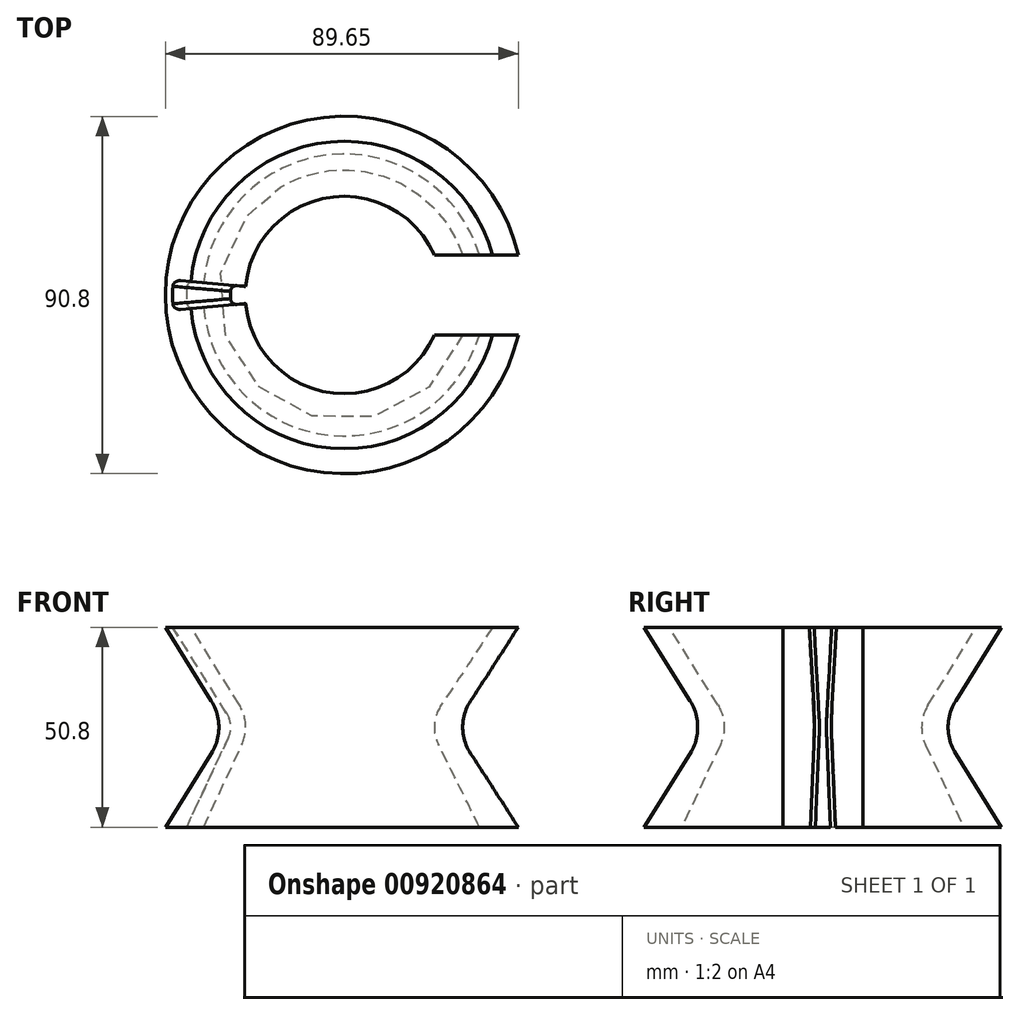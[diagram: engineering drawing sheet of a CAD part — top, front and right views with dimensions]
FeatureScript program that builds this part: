
annotation { "Feature Type Name" : "Feature", "Feature Type Description" : "" }
export const myFeature = defineFeature(function(context is Context, id is Id, definition is map)
    precondition{}
    {
        {
            var Q0;
            Q0=qCreatedBy(makeId("Front.planeOp"),FACE);
            var sketch = newSketch(context, id + "F0", { "sketchPlane" : qUnion([Q0])});
            skLineSegment(sketch, "E0", {"start": v(25.08, -16.33) * mm, "end": v(25.08, 0) * mm, "construction": true});
            skArc(sketch, "E1", {"start": v(26.7, 5.62) * mm, "mid": v(25.1, 0.65) * mm, "end": v(26.08, -4.48) * mm});
            skLineSegment(sketch, "E2", {"start": v(39.05, 25.4) * mm, "end": v(26.7, 5.62) * mm});
            skLineSegment(sketch, "E3", {"start": v(35.83, -25.4) * mm, "end": v(26.08, -4.48) * mm});
            skLineSegment(sketch, "E4", {"start": v(39.05, 25.4) * mm, "end": v(45.4, 25.4) * mm});
            skLineSegment(sketch, "E5", {"start": v(45.4, 25.4) * mm, "end": v(45.4, -25.4) * mm, "construction": true});
            skLineSegment(sketch, "E6", {"start": v(45.4, -25.4) * mm, "end": v(35.83, -25.4) * mm});
            skLineSegment(sketch, "E7", {"start": v(0, 56.75) * mm, "end": v(0, -54.17) * mm, "construction": true});
            skLineSegment(sketch, "E8", {"start": v(45.4, 25.4) * mm, "end": v(33.74, 6.73) * mm});
            skLineSegment(sketch, "E9", {"start": v(33.74, -6.73) * mm, "end": v(45.4, -25.4) * mm});
            skPoint(sketch, "E10.visualSharp", {"position": v(29.53, 0) * mm});
            skArc(sketch, "E10.filletArc", {"start": v(33.74, 6.73) * mm, "mid": v(31.8, 0) * mm, "end": v(33.74, -6.73) * mm});
            skSolve(sketch);
        }
        {
            var Q0;
            Q0 = qSketchRegion(id + "F0", true);
            var Q1;
            Q1=sQuery(id+"F0.wireOp",EDGE,"E7");
            revolve(context, id + "F1", {"surfaceOperationType" : NewSurfaceOperationType.NEW, "entities" : qUnion([Q0]), "axis" : qUnion([Q1]), "revolveType" : RevolveType.FULL});
        }
        {
            var Q0;
            Q0=qCreatedBy(makeId("Front.planeOp"),FACE);
            var sketch = newSketch(context, id + "F2", { "sketchPlane" : qUnion([Q0])});
            skLineSegment(sketch, "E11", {"start": v(-26.7, 5.62) * mm, "end": v(-39.05, 25.4) * mm});
            skArc(sketch, "E12", {"start": v(-26.08, -4.48) * mm, "mid": v(-25.1, 0.65) * mm, "end": v(-26.7, 5.62) * mm});
            skLineSegment(sketch, "E13", {"start": v(-35.83, -25.4) * mm, "end": v(-26.08, -4.48) * mm});
            skLineSegment(sketch, "E14.0", {"start": v(-29.92, 3.6) * mm, "end": v(-43.55, 25.4) * mm});
            skArc(sketch, "E14.1", {"start": v(-29.53, -2.87) * mm, "mid": v(-28.9, 0.41) * mm, "end": v(-29.92, 3.6) * mm});
            skLineSegment(sketch, "E14.2", {"start": v(-40.03, -25.4) * mm, "end": v(-29.53, -2.87) * mm});
            skLineSegment(sketch, "E15", {"start": v(-39.05, 25.4) * mm, "end": v(-43.55, 25.4) * mm});
            skLineSegment(sketch, "E16", {"start": v(-40.03, -25.4) * mm, "end": v(-35.83, -25.4) * mm});
            skLineSegment(sketch, "E17", {"start": v(0, 8.2) * mm, "end": v(0, 37.86) * mm, "construction": true});
            skSolve(sketch);
        }
        {
            var Q0;
            Q0 = qSketchRegion(id + "F2", true);
            var Q1;
            Q1=sQuery(id+"F2.wireOp",EDGE,"E17");
            revolve(context, id + "F3", {"operationType" : NewBodyOperationType.REMOVE, "surfaceOperationType" : NewSurfaceOperationType.NEW, "entities" : qUnion([Q0]), "axis" : qUnion([Q1]), "revolveType" : RevolveType.SYMMETRIC, "oppositeDirection" : true, "angle" : 10 * degree});
        }
        {
            var Q0;
            Q0=makeQuery(id+"F3.boolean.opBoolean","COPY",EDGE,{"derivedFrom":makeQuery(id+"F3.opRevolve","CAP_EDGE",EDGE,{"disambiguationData":[OSD([sQuery(id+"F2.wireOp",EDGE,"E11")])],"isStart":false})});
            var Q1;
            Q1=makeQuery(id+"F3.boolean.opBoolean","COPY",EDGE,{"derivedFrom":makeQuery(id+"F3.opRevolve","CAP_EDGE",EDGE,{"disambiguationData":[OSD([sQuery(id+"F2.wireOp",EDGE,"E14.0")])],"isStart":false})});
            var Q2;
            Q2=makeQuery(id+"F3.boolean.opBoolean","COPY",EDGE,{"derivedFrom":makeQuery(id+"F3.opRevolve","CAP_EDGE",EDGE,{"disambiguationData":[OSD([sQuery(id+"F2.wireOp",EDGE,"E14.0")])],"isStart":true})});
            var Q3;
            Q3=makeQuery(id+"F3.boolean.opBoolean","COPY",EDGE,{"derivedFrom":makeQuery(id+"F3.opRevolve","CAP_EDGE",EDGE,{"disambiguationData":[OSD([sQuery(id+"F2.wireOp",EDGE,"E11")])],"isStart":true})});
            fillet(context, id + "F4", {"entities" : qUnion([Q0, Q1, Q2, Q3]), "radius" : 1.52 * mm, "tangentPropagation" : true, "allowEdgeOverflow" : false});
        }
        {
            var Q0;
            Q0=makeQuery(id+"F1.opRevolve","SWEPT_FACE",FACE,{"disambiguationData":[OSD([sQuery(id+"F0.wireOp",EDGE,"E4")])]});
            var sketch = newSketch(context, id + "F5", { "sketchPlane" : qUnion([Q0])});
            skLineSegment(sketch, "E18.bottom", {"start": v(15.33, 10.16) * mm, "end": v(104.52, 10.16) * mm});
            skLineSegment(sketch, "E18.top", {"start": v(15.33, -10.16) * mm, "end": v(104.52, -10.16) * mm});
            skLineSegment(sketch, "E18.left", {"start": v(15.33, 10.16) * mm, "end": v(15.33, -10.16) * mm});
            skLineSegment(sketch, "E18.right", {"start": v(104.52, 10.16) * mm, "end": v(104.52, -10.16) * mm});
            skPoint(sketch, "E18.middle", {"position": v(59.93, 0) * mm});
            skSolve(sketch);
        }
        {
            var Q0;
            Q0 = qSketchRegion(id + "F5", true);
            extrude(context, id + "F6", {"entities" : qUnion([Q0]), "operationType" : NewBodyOperationType.REMOVE, "endBound" : BoundingType.THROUGH_ALL, "oppositeDirection" : true, "depth" : 25.4 * mm, "offsetDistance" : 25.4 * mm});
        }
    });
